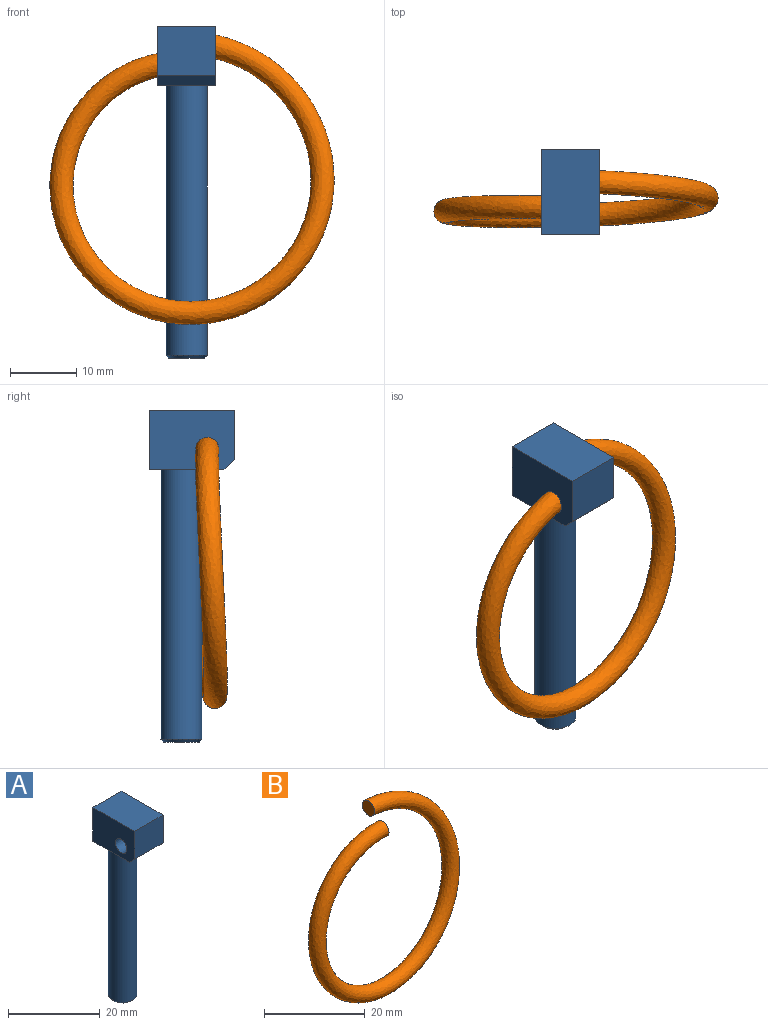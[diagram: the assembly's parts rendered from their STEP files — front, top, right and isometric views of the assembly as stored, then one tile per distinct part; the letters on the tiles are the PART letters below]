
ASSEMBLY  parts=2 mates=1
PART A: 14 faces, bbox 10.4x13.7x50.9 mm
  f0: cylinder r=3.1mm len=40.61mm, axis (0,0,1), area 790.8mm2, adj f3,f13
  f1: plane 5.44x5.44mm, normal (0,0,-1), area 23.2mm2, adj f13
  f2: plane 8.79x1.59mm, normal (0,-0.71,-0.71), area 19.7mm2, adj f3,f6,f7,f8
  f3: plane 11.21x8.79mm, normal (0,0,-1), area 68.4mm2, adj f0,f2,f4,f7,f8
  f4: plane 8.99x8.79mm, normal (0,1,0), area 79mm2, adj f3,f5,f7,f8
  f5: plane 12.8x8.79mm, normal (0,0,1), area 112.5mm2, adj f4,f6,f7,f8
  f6: plane 8.79x7.4mm, normal (0,-1,0), area 65.1mm2, adj f2,f5,f7,f8
  f7: plane 13.57x9.76mm, normal (1,0,0), area 104mm2, adj f2,f3,f4,f5,f6,f12
  f8: plane 13.67x9.86mm, normal (-1,0,0), area 104mm2, adj f2,f3,f4,f5,f6,f10
  f9: plane 4x4mm, normal (-1,0,0), area 9.6mm2, adj f10
  f10: bspline ~4.81x3.84mm, area 48.8mm2, adj f8,f9
  f11: plane 3.99x3.99mm, normal (1,0,0), area 9.6mm2, adj f12
  f12: bspline ~4.76x3.98mm, area 49mm2, adj f7,f11
  f13: cone r=3.1mm half-angle=45deg, axis (0,0,1), area 9.8mm2, adj f0,f1
PART B: 3 faces, bbox 43.2x9.2x44.6 mm
  f0: plane 3.99x3.99mm, normal (-1,0,0), area 9.6mm2, adj f2
  f1: plane 4x4mm, normal (1,0,0), area 9.6mm2, adj f2
  f2: bspline ~44.05x42.73mm, area 1358.9mm2, adj f0,f1
PLACE A at identity fixed
PLACE B at identity
MATE revolute B.f0 <-> A.f11  axis (-1,0,0) through (0,0,6.4)mm
